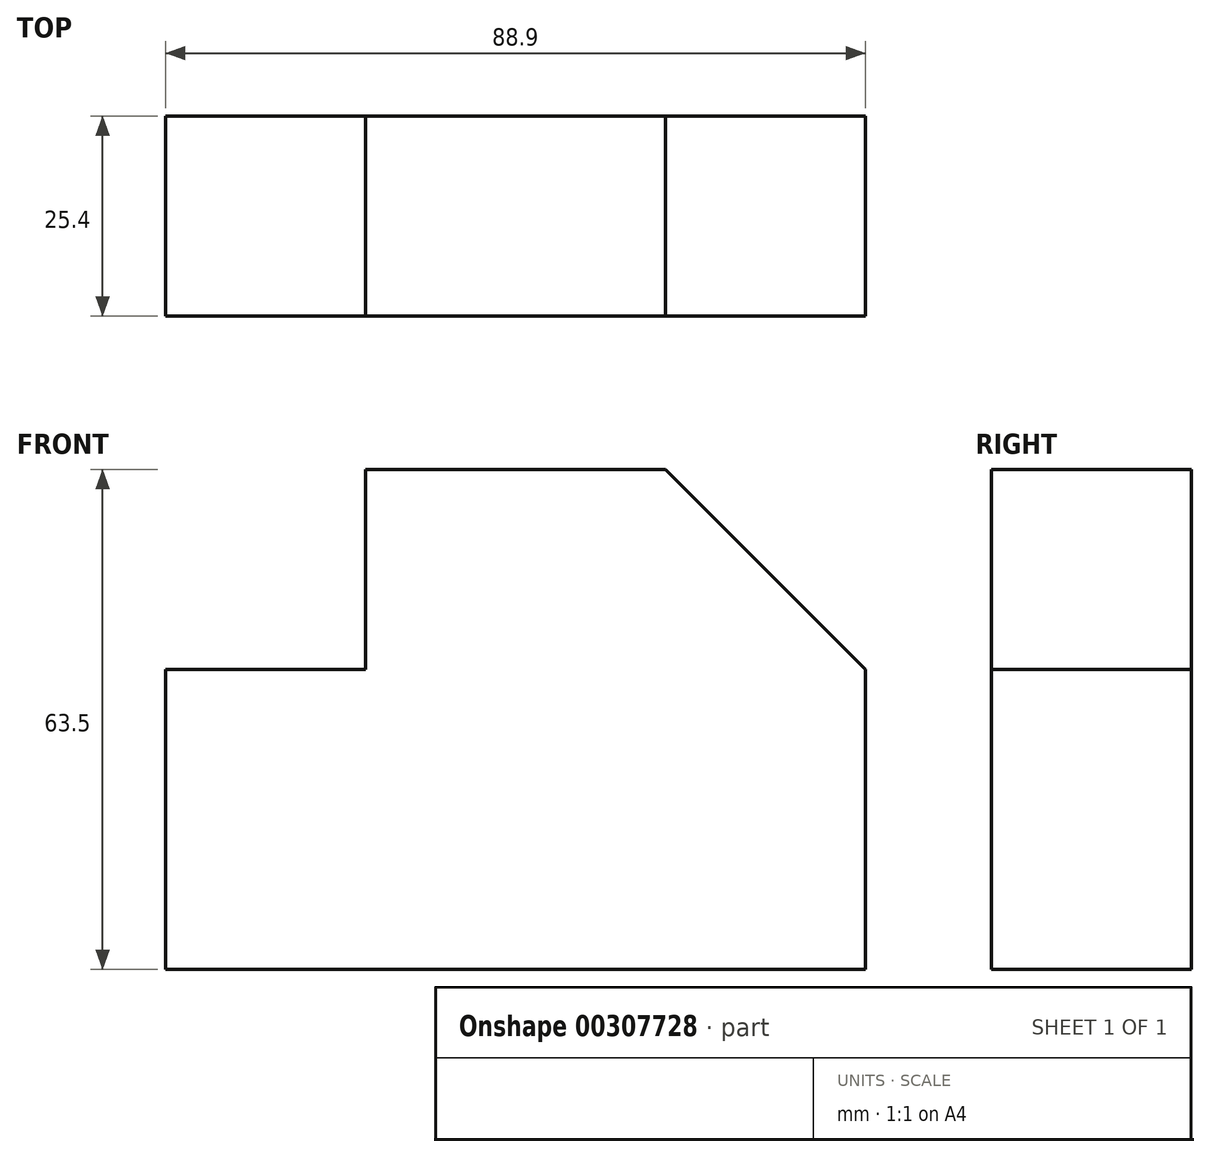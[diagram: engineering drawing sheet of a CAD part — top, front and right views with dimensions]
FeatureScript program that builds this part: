
annotation { "Feature Type Name" : "Feature", "Feature Type Description" : "" }
export const myFeature = defineFeature(function(context is Context, id is Id, definition is map)
    precondition{}
    {
        {
            var Q0;
            Q0=qCreatedBy(makeId("Front.planeOp"),FACE);
            var sketch = newSketch(context, id + "F0", { "sketchPlane" : qUnion([Q0])});
            skLineSegment(sketch, "E0", {"start": v(42.28, -16.68) * mm, "end": v(42.28, -54.78) * mm});
            skLineSegment(sketch, "E1", {"start": v(42.28, -54.78) * mm, "end": v(-46.62, -54.78) * mm});
            skLineSegment(sketch, "E2", {"start": v(-46.62, -54.78) * mm, "end": v(-46.62, -16.68) * mm});
            skLineSegment(sketch, "E3", {"start": v(-46.62, -16.68) * mm, "end": v(-21.22, -16.68) * mm});
            skLineSegment(sketch, "E4", {"start": v(-21.22, -16.68) * mm, "end": v(-21.22, 8.72) * mm});
            skLineSegment(sketch, "E5", {"start": v(-21.22, 8.72) * mm, "end": v(16.88, 8.72) * mm});
            skLineSegment(sketch, "E6", {"start": v(16.88, 8.72) * mm, "end": v(42.28, -16.68) * mm});
            skSolve(sketch);
        }
        {
            var Q0;
            Q0=makeQuery(id+"F0.imprint","IMPRINT",FACE,{"disambiguationData":[TD([[makeQuery(id+"F0.imprint","IMPRINT",EDGE,{"derivedFrom":sQuery(id+"F0.wireOp",EDGE,"E0")}),-1.0]])]});
            extrude(context, id + "F1", {"entities" : qUnion([Q0]), "depth" : 25.4 * mm});
        }
    });
